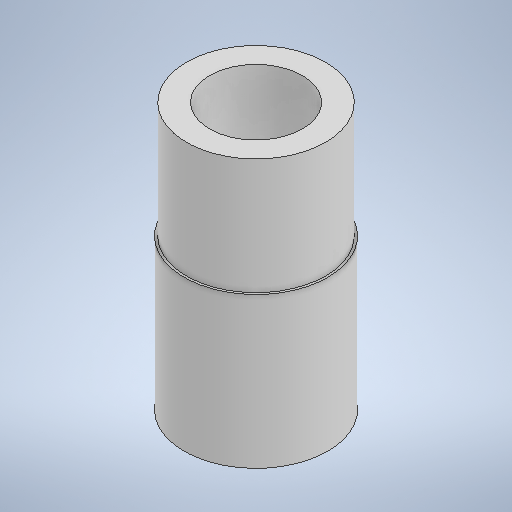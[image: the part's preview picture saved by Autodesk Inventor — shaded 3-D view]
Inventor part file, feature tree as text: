
AUTODESK INVENTOR PART (.ipt)
format: ipt  version: 2025.3 (Build 293356030, 356C)  size: 239,104 bytes
history: native  units: mm
features: extrude x3, sketch x3, other x1
ambient origin geometry x8: Origin, YZ Plane, XZ Plane, XY Plane, X Axis, Y Axis, Z Axis, Center Point
bodies: Body1 (feature_tree)
feature tree (7):
  other  "Sólido1"
  extrude  "Extrusión1"  Depth=11.5mm TaperAngle=0.0deg
  extrude  "Extrusión2"  Depth=15.75mm TaperAngle=0.0deg
  extrude  "Extrusión3"  Depth=5.0mm TaperAngle=0.0deg
  sketch  "Boceto1"  dims[d0=6.2mm d1=11.5mm d2=0.0mm]
  sketch  "Boceto2"  dims[d3=4.0mm d4=15.75mm d5=0.0mm]
  sketch  "Boceto3"  dims[d6=6.0mm d7=5.0mm d8=0.0mm]
